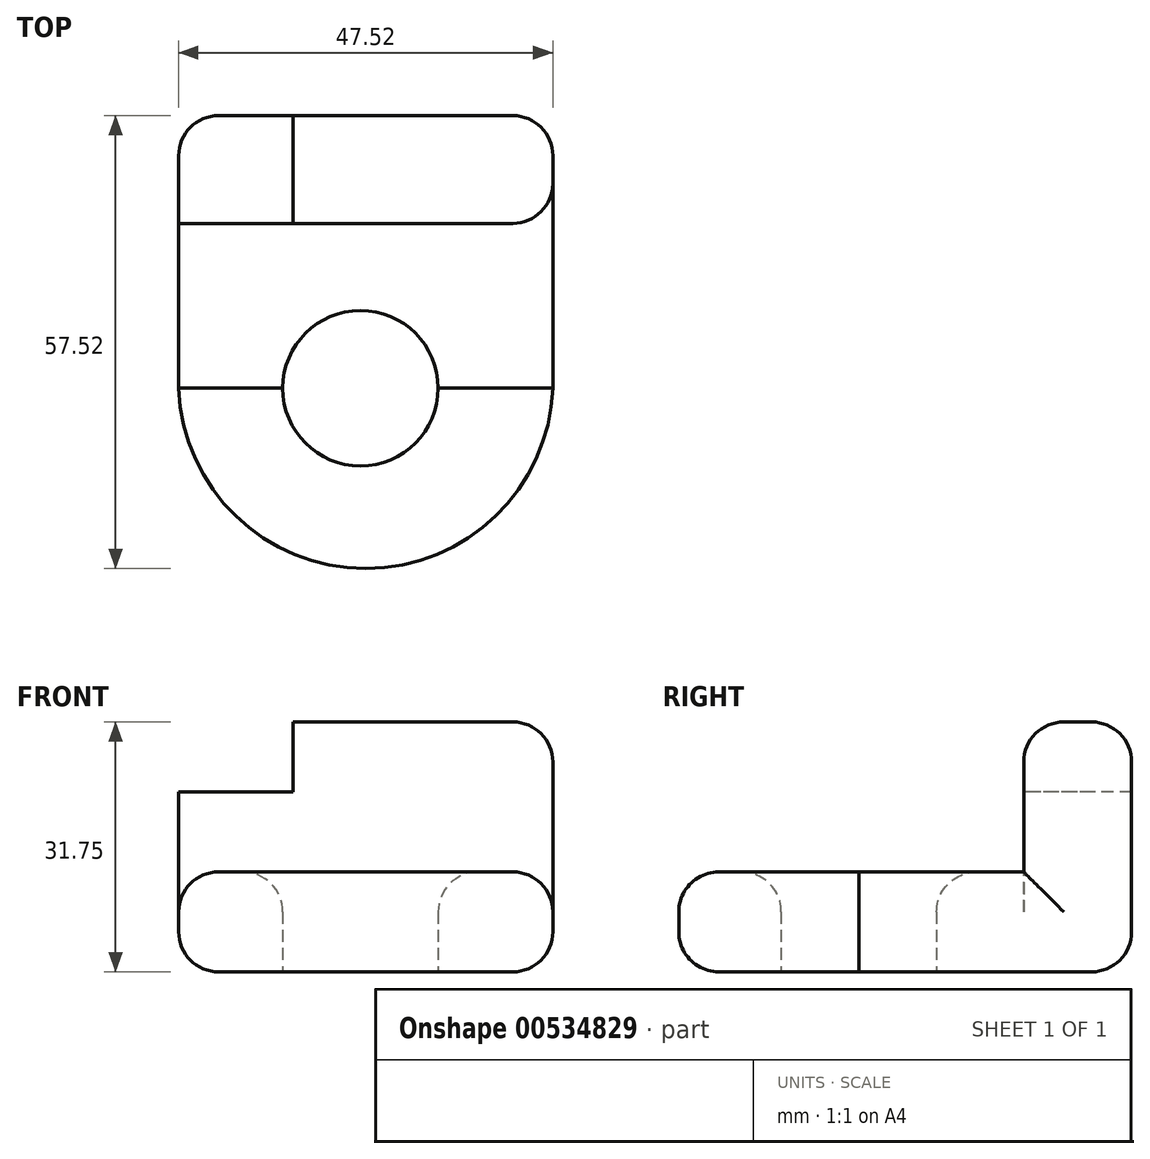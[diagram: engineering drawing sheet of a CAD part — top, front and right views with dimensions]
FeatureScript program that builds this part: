
annotation { "Feature Type Name" : "Feature", "Feature Type Description" : "" }
export const myFeature = defineFeature(function(context is Context, id is Id, definition is map)
    precondition{}
    {
        {
            var Q0;
            Q0=qCreatedBy(makeId("Top.planeOp"),FACE);
            var sketch = newSketch(context, id + "F0", { "sketchPlane" : qUnion([Q0])});
            skArc(sketch, "E0", {"start": v(-23.1, 0) * mm, "mid": v(0.67, -22.89) * mm, "end": v(24.43, 0) * mm});
            skLineSegment(sketch, "E1", {"start": v(-23.1, 0) * mm, "end": v(24.43, 0) * mm});
            skSolve(sketch);
        }
        {
            var Q0;
            Q0=qCreatedBy(makeId("Top.planeOp"),FACE);
            var sketch = newSketch(context, id + "F1", { "sketchPlane" : qUnion([Q0])});
            skLineSegment(sketch, "E2.bottom", {"start": v(-23.1, 34.63) * mm, "end": v(24.43, 34.63) * mm});
            skLineSegment(sketch, "E2.top", {"start": v(-23.1, 0) * mm, "end": v(24.43, 0) * mm});
            skLineSegment(sketch, "E2.left", {"start": v(-23.1, 34.63) * mm, "end": v(-23.1, 0) * mm});
            skLineSegment(sketch, "E2.right", {"start": v(24.43, 34.63) * mm, "end": v(24.43, 0) * mm});
            skSolve(sketch);
        }
        {
            var Q0;
            Q0=makeQuery(id+"F0.imprint","IMPRINT",FACE,{"disambiguationData":[TD([[makeQuery(id+"F0.imprint","IMPRINT",EDGE,{"derivedFrom":sQuery(id+"F0.wireOp",EDGE,"E0")}),1.0]])]});
            var Q1;
            Q1=makeQuery(id+"F1.imprint","IMPRINT",FACE,{"disambiguationData":[TD([[makeQuery(id+"F1.imprint","IMPRINT",EDGE,{"derivedFrom":sQuery(id+"F1.wireOp",EDGE,"E2.bottom")}),-1.0]])]});
            extrude(context, id + "F2", {"entities" : qUnion([Q0, Q1]), "depth" : 12.7 * mm, "offsetDistance" : 25.4 * mm});
        }
        {
            var Q0;
            Q0=makeQuery(id+"F2.opExtrude","CAP_FACE",FACE,{"disambiguationData":[OSD([sQuery(id+"F1.wireOp",EDGE,"E2.bottom"),sQuery(id+"F1.wireOp",EDGE,"E2.top"),sQuery(id+"F1.wireOp",EDGE,"E2.left"),sQuery(id+"F1.wireOp",EDGE,"E2.right")])],"isStart":false});
            var sketch = newSketch(context, id + "F3", { "sketchPlane" : qUnion([Q0])});
            skLineSegment(sketch, "E3.bottom", {"start": v(-23.1, 34.63) * mm, "end": v(24.43, 34.63) * mm});
            skLineSegment(sketch, "E3.top", {"start": v(-23.1, 20.94) * mm, "end": v(24.43, 20.94) * mm});
            skLineSegment(sketch, "E3.left", {"start": v(-23.1, 34.63) * mm, "end": v(-23.1, 20.94) * mm});
            skLineSegment(sketch, "E3.right", {"start": v(24.43, 34.63) * mm, "end": v(24.43, 20.94) * mm});
            skSolve(sketch);
        }
        {
            var Q0;
            Q0 = qSketchRegion(id + "F3", true);
            extrude(context, id + "F4", {"entities" : qUnion([Q0]), "operationType" : NewBodyOperationType.ADD, "depth" : 19.05 * mm, "offsetDistance" : 25.4 * mm});
        }
        {
            var Q0;
            Q0=makeQuery(id+"F4.opExtrude","CAP_FACE",FACE,{"disambiguationData":[OSD([sQuery(id+"F3.wireOp",EDGE,"E3.bottom"),sQuery(id+"F3.wireOp",EDGE,"E3.top"),sQuery(id+"F3.wireOp",EDGE,"E3.left"),sQuery(id+"F3.wireOp",EDGE,"E3.right")])],"isStart":false});
            var sketch = newSketch(context, id + "F5", { "sketchPlane" : qUnion([Q0])});
            skLineSegment(sketch, "E4.bottom", {"start": v(-23.1, 34.63) * mm, "end": v(-8.6, 34.63) * mm});
            skLineSegment(sketch, "E4.top", {"start": v(-23.1, 20.94) * mm, "end": v(-8.6, 20.94) * mm});
            skLineSegment(sketch, "E4.left", {"start": v(-23.1, 34.63) * mm, "end": v(-23.1, 20.94) * mm});
            skLineSegment(sketch, "E4.right", {"start": v(-8.6, 34.63) * mm, "end": v(-8.6, 20.94) * mm});
            skSolve(sketch);
        }
        {
            var Q0;
            Q0 = qSketchRegion(id + "F5", true);
            extrude(context, id + "F6", {"entities" : qUnion([Q0]), "operationType" : NewBodyOperationType.REMOVE, "oppositeDirection" : true, "depth" : 8.9 * mm, "offsetDistance" : 25.4 * mm});
        }
        {
            var Q0;
            Q0=qCreatedBy(makeId("Top.planeOp"),FACE);
            var sketch = newSketch(context, id + "F7", { "sketchPlane" : qUnion([Q0])});
            skCircle(sketch, "E5", {"center": v(0, 0) * mm, "radius": 9.87 * mm});
            skSolve(sketch);
        }
        {
            var Q0;
            Q0 = qSketchRegion(id + "F7", true);
            extrude(context, id + "F8", {"entities" : qUnion([Q0]), "operationType" : NewBodyOperationType.REMOVE, "endBound" : BoundingType.THROUGH_ALL, "depth" : 25.4 * mm, "offsetDistance" : 25.4 * mm});
        }
        {
            var Q0;
            Q0=makeQuery(id+"F8.boolean.opBoolean","INTERSECT",EDGE,{"derivedFrom":[makeQuery(id+"F2.opExtrude","CAP_FACE",FACE,{"disambiguationData":[OSD([sQuery(id+"F1.wireOp",EDGE,"E2.bottom"),sQuery(id+"F1.wireOp",EDGE,"E2.top"),sQuery(id+"F1.wireOp",EDGE,"E2.left"),sQuery(id+"F1.wireOp",EDGE,"E2.right")])],"isStart":false}),makeQuery(id+"F8.opExtrude","SWEPT_FACE",FACE,{"disambiguationData":[OSD([sQuery(id+"F7.wireOp",EDGE,"E5")])]})]});
            var Q1;
            Q1=makeQuery(id+"F8.boolean.opBoolean","INTERSECT",EDGE,{"derivedFrom":[makeQuery(id+"F2.opExtrude","CAP_FACE",FACE,{"disambiguationData":[OSD([sQuery(id+"F0.wireOp",EDGE,"E0"),sQuery(id+"F0.wireOp",EDGE,"E1")])],"isStart":false}),makeQuery(id+"F8.opExtrude","SWEPT_FACE",FACE,{"disambiguationData":[OSD([sQuery(id+"F7.wireOp",EDGE,"E5")])]})]});
            var Q2;
            {var subQ0=sQuery(id+"F7.wireOp",EDGE,"E5");Q2=makeQuery(id+"F8.boolean.opBoolean","COPY",EDGE,{"disambiguationData":[topologyDisambiguationEdgeConnected([makeQuery(id+"F2.opExtrude","CAP_FACE",FACE,{"disambiguationData":[OSD([sQuery(id+"F0.wireOp",EDGE,"E0"),sQuery(id+"F0.wireOp",EDGE,"E1")])],"isStart":true})])],"derivedFrom":makeQuery(id+"F8.opExtrude","CAP_EDGE",EDGE,{"disambiguationData":[OSD([subQ0])],"isStart":true})});}
            var Q3;
            {var subQ0=sQuery(id+"F7.wireOp",EDGE,"E5");Q3=makeQuery(id+"F8.boolean.opBoolean","COPY",EDGE,{"disambiguationData":[topologyDisambiguationEdgeConnected([makeQuery(id+"F2.opExtrude","CAP_FACE",FACE,{"disambiguationData":[OSD([sQuery(id+"F1.wireOp",EDGE,"E2.bottom"),sQuery(id+"F1.wireOp",EDGE,"E2.top"),sQuery(id+"F1.wireOp",EDGE,"E2.left"),sQuery(id+"F1.wireOp",EDGE,"E2.right")])],"isStart":true})])],"derivedFrom":makeQuery(id+"F8.opExtrude","CAP_EDGE",EDGE,{"disambiguationData":[OSD([subQ0])],"isStart":true})});}
            var Q4;
            Q4=makeQuery(id+"F2.opExtrude","CAP_EDGE",EDGE,{"disambiguationData":[OSD([sQuery(id+"F0.wireOp",EDGE,"E0")])],"isStart":false});
            var Q5;
            Q5=makeQuery(id+"F2.opExtrude","CAP_EDGE",EDGE,{"disambiguationData":[OSD([sQuery(id+"F0.wireOp",EDGE,"E0")])],"isStart":true});
            var Q6;
            Q6=makeQuery(id+"F2.opExtrude","CAP_EDGE",EDGE,{"disambiguationData":[OSD([sQuery(id+"F1.wireOp",EDGE,"E2.left")])],"isStart":false});
            var Q7;
            Q7=makeQuery(id+"F2.opExtrude","CAP_EDGE",EDGE,{"disambiguationData":[OSD([sQuery(id+"F1.wireOp",EDGE,"E2.right")])],"isStart":false});
            var Q8;
            Q8=makeQuery(id+"F2.opExtrude","CAP_EDGE",EDGE,{"disambiguationData":[OSD([sQuery(id+"F1.wireOp",EDGE,"E2.right")])],"isStart":true});
            var Q9;
            Q9=makeQuery(id+"F2.opExtrude","CAP_EDGE",EDGE,{"disambiguationData":[OSD([sQuery(id+"F1.wireOp",EDGE,"E2.left")])],"isStart":true});
            var Q10;
            Q10=makeQuery(id+"F2.opExtrude","CAP_EDGE",EDGE,{"disambiguationData":[OSD([sQuery(id+"F1.wireOp",EDGE,"E2.bottom")])],"isStart":true});
            fillet(context, id + "F9", {"entities" : qUnion([Q0, Q1, Q2, Q3, Q4, Q5, Q6, Q7, Q8, Q9, Q10]), "radius" : 5.08 * mm, "tangentPropagation" : true, "allowEdgeOverflow" : false});
        }
        {
            var Q0;
            Q0=makeQuery(id+"F4.opExtrude","CAP_EDGE",EDGE,{"disambiguationData":[OSD([sQuery(id+"F3.wireOp",EDGE,"E3.top")])],"isStart":false});
            var Q1;
            Q1=makeQuery(id+"F6.boolean.opBoolean","COPY",EDGE,{"derivedFrom":makeQuery(id+"F6.opExtrude","CAP_EDGE",EDGE,{"disambiguationData":[OSD([sQuery(id+"F5.wireOp",EDGE,"E4.top")])],"isStart":false})});
            var Q2;
            Q2=makeQuery(id+"F6.boolean.opBoolean","COPY",EDGE,{"derivedFrom":makeQuery(id+"F6.opExtrude","CAP_EDGE",EDGE,{"disambiguationData":[OSD([sQuery(id+"F5.wireOp",EDGE,"E4.right")])],"isStart":true})});
            var Q3;
            Q3=makeQuery(id+"F4.opExtrude","CAP_EDGE",EDGE,{"disambiguationData":[OSD([sQuery(id+"F3.wireOp",EDGE,"E3.bottom")])],"isStart":false});
            var Q4;
            Q4=makeQuery(id+"F4.opExtrude","CAP_EDGE",EDGE,{"disambiguationData":[OSD([sQuery(id+"F3.wireOp",EDGE,"E3.right")])],"isStart":false});
            var Q5;
            Q5=makeQuery(id+"F6.boolean.opBoolean","COPY",EDGE,{"derivedFrom":makeQuery(id+"F6.opExtrude","CAP_EDGE",EDGE,{"disambiguationData":[OSD([sQuery(id+"F5.wireOp",EDGE,"E4.bottom")])],"isStart":false})});
            var Q6;
            Q6=makeQuery(id+"F6.boolean.opBoolean","COPY",EDGE,{"derivedFrom":makeQuery(id+"F6.opExtrude","CAP_EDGE",EDGE,{"disambiguationData":[OSD([sQuery(id+"F5.wireOp",EDGE,"E4.left")])],"isStart":false})});
            var Q7;
            Q7=makeQuery(id+"F4.boolean.opBoolean","MERGE",EDGE,{"derivedFrom":[makeQuery(id+"F2.opExtrude","SWEPT_EDGE",EDGE,{"disambiguationData":[OSD([sQuery(id+"F1.wireOp",EDGE,"E2.bottom"),sQuery(id+"F1.wireOp",EDGE,"E2.left")])]}),makeQuery(id+"F4.opExtrude","SWEPT_EDGE",EDGE,{"disambiguationData":[OSD([sQuery(id+"F3.wireOp",EDGE,"E3.bottom"),sQuery(id+"F3.wireOp",EDGE,"E3.left")])]})]});
            var Q8;
            Q8=makeQuery(id+"F4.boolean.opBoolean","MERGE",EDGE,{"derivedFrom":[makeQuery(id+"F2.opExtrude","SWEPT_EDGE",EDGE,{"disambiguationData":[OSD([sQuery(id+"F1.wireOp",EDGE,"E2.bottom"),sQuery(id+"F1.wireOp",EDGE,"E2.right")])]}),makeQuery(id+"F4.opExtrude","SWEPT_EDGE",EDGE,{"disambiguationData":[OSD([sQuery(id+"F3.wireOp",EDGE,"E3.bottom"),sQuery(id+"F3.wireOp",EDGE,"E3.right")])]})]});
            var Q9;
            Q9=makeQuery(id+"F4.opExtrude","SWEPT_EDGE",EDGE,{"disambiguationData":[OSD([sQuery(id+"F1.wireOp",EDGE,"E2.right"),sQuery(id+"F3.wireOp",EDGE,"E3.top"),sQuery(id+"F3.wireOp",EDGE,"E3.right")])]});
            fillet(context, id + "F10", {"entities" : qUnion([Q0, Q1, Q2, Q3, Q4, Q5, Q6, Q7, Q8, Q9]), "radius" : 5.08 * mm, "tangentPropagation" : true, "allowEdgeOverflow" : false});
        }
    });
